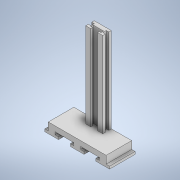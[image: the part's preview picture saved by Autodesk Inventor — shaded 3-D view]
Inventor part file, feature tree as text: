
AUTODESK INVENTOR PART (.ipt)
format: ipt  version: 2022 (Build 260153000, 153)  size: 199,680 bytes
history: native  units: mm
features: sketch x5, extrude x4
ambient origin geometry x8: Origin, YZ Plane, XZ Plane, XY Plane, X Axis, Y Axis, Z Axis, Center Point
bodies: Solid1 (feature_tree)
feature tree (9):
  sketch  "Sketch1"  dims[d0=300.0mm d1=600.0mm d2=50.0mm d3=50.0mm d4=20.0mm d5=20.0mm d6=20.0mm d7=20.0mm d8=30.0mm d9=15.0mm d10=15.0mm d11=75.0mm d12=75.0mm d13=15.0mm d14=109.793049mm d15=142.819914mm d16=109.793049mm d17=147.872174mm d18=45.0mm]
  sketch  "Sketch2"  dims[d19=150.0mm d20=0.0mm d21=40.0mm]
  extrude  "Extrusion1"  Depth=45.0mm
  extrude  "Extrusion2"  Depth=40.0mm
  extrude  "Extrusion3"  Depth=40.0mm
  extrude  "Extrusion4"  Depth=10.0mm
  sketch  "Sketch3"  dims[d22=50.0mm d23=40.0mm]
  sketch  "Sketch5"  dims[d24=500.0mm d25=0.0mm d26=10.0mm]
  sketch  "Sketch6"  dims[d27=15.0mm d28=60.0mm d29=500.0mm d30=0.0mm d31=20.0mm d34=500.0mm d35=0.0mm d36=100.0mm d38=5.0mm d39=15.0mm d32=0.872665mm]
